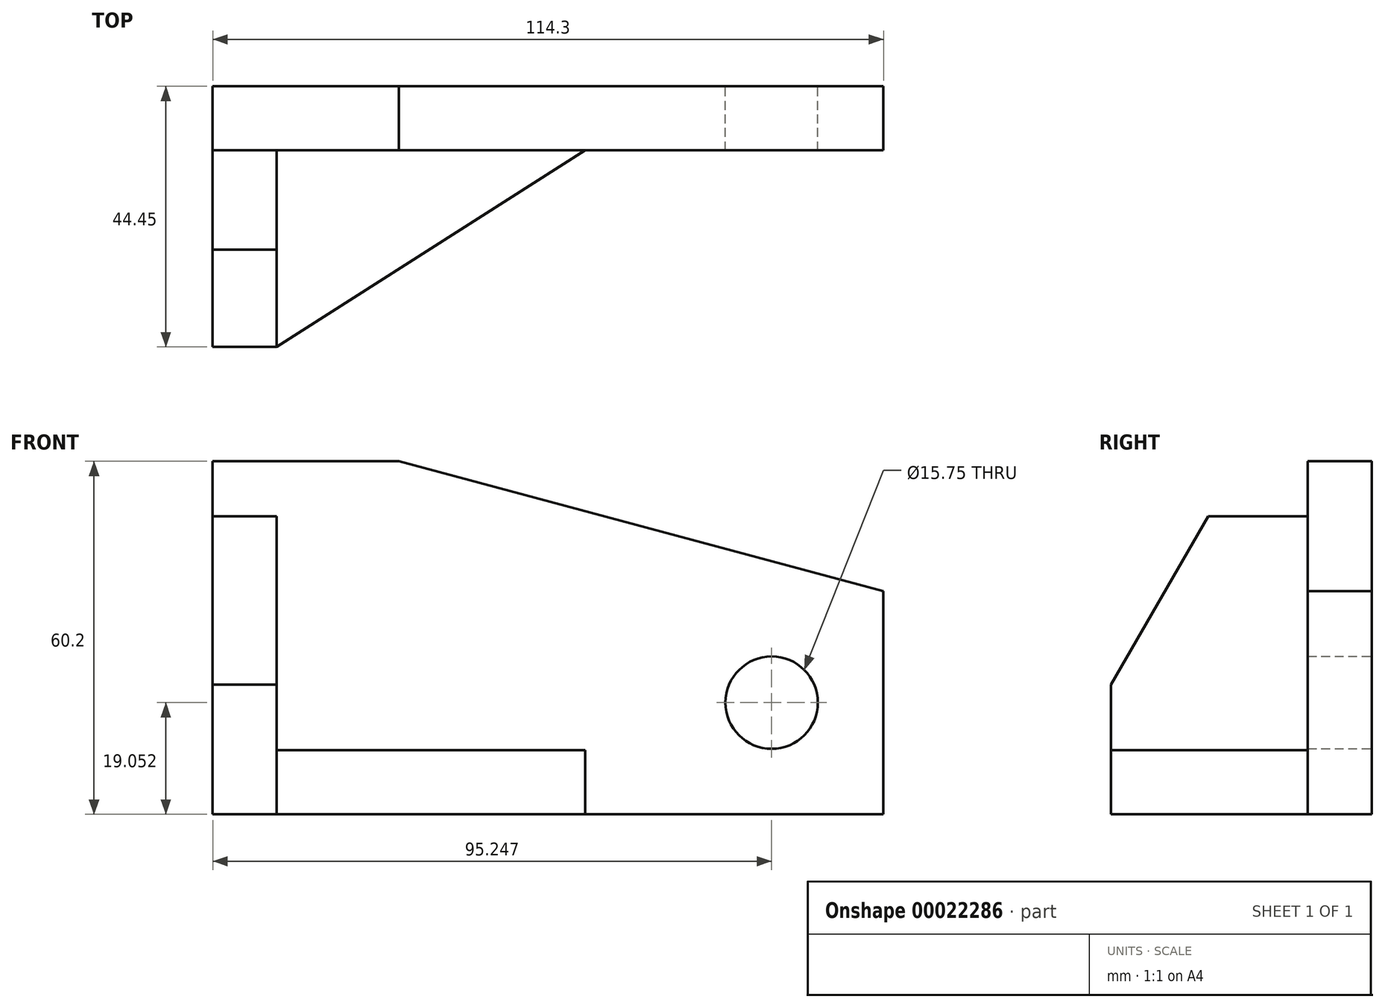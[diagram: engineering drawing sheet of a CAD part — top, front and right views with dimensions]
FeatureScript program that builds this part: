
annotation { "Feature Type Name" : "Feature", "Feature Type Description" : "" }
export const myFeature = defineFeature(function(context is Context, id is Id, definition is map)
    precondition{}
    {
        {
            var Q0;
            Q0=qCreatedBy(makeId("Front.planeOp"),FACE);
            var sketch = newSketch(context, id + "F0", { "sketchPlane" : qUnion([Q0])});
            skLineSegment(sketch, "E0.bottom", {"start": v(-81.32, 43.66) * mm, "end": v(32.98, 43.66) * mm});
            skLineSegment(sketch, "E0.top", {"start": v(-81.32, -16.54) * mm, "end": v(32.98, -16.54) * mm});
            skLineSegment(sketch, "E0.left", {"start": v(-81.32, 43.66) * mm, "end": v(-81.32, -16.54) * mm});
            skLineSegment(sketch, "E0.right", {"start": v(32.98, 43.66) * mm, "end": v(32.98, -16.54) * mm});
            skLineSegment(sketch, "E1", {"start": v(-49.57, 43.66) * mm, "end": v(32.98, 21.54) * mm});
            skCircle(sketch, "E2", {"center": v(13.93, 2.51) * mm, "radius": 7.87 * mm});
            skSolve(sketch);
        }
        {
            var Q0;
            {var subQ2=sQuery(id+"F0.wireOp",EDGE,"E0.top");Q0=makeQuery(id+"F0.imprint","IMPRINT",FACE,{"disambiguationData":[TD([[makeQuery(id+"F0.imprint","IMPRINT",EDGE,{"derivedFrom":subQ2}),1.0]])]});}
            extrude(context, id + "F1", {"entities" : qUnion([Q0]), "depth" : 10.92 * mm});
        }
        {
            var Q0;
            Q0=makeQuery(id+"F1.opExtrude","CAP_FACE",FACE,{"disambiguationData":[OSD([sQuery(id+"F0.wireOp",EDGE,"E0.bottom"),sQuery(id+"F0.wireOp",EDGE,"E0.top"),sQuery(id+"F0.wireOp",EDGE,"E0.left"),sQuery(id+"F0.wireOp",EDGE,"E0.right"),sQuery(id+"F0.wireOp",EDGE,"E1")])],"isStart":false});
            var sketch = newSketch(context, id + "F2", { "sketchPlane" : qUnion([Q0])});
            skLineSegment(sketch, "E3.bottom", {"start": v(-81.32, 34.26) * mm, "end": v(-70.4, 34.26) * mm});
            skLineSegment(sketch, "E3.top", {"start": v(-81.32, -16.54) * mm, "end": v(-70.4, -16.54) * mm});
            skLineSegment(sketch, "E3.left", {"start": v(-81.32, 34.26) * mm, "end": v(-81.32, -16.54) * mm});
            skLineSegment(sketch, "E3.right", {"start": v(-70.4, 34.26) * mm, "end": v(-70.4, -16.54) * mm});
            skSolve(sketch);
        }
        {
            var Q0;
            Q0 = qSketchRegion(id + "F2", true);
            extrude(context, id + "F3", {"entities" : qUnion([Q0]), "operationType" : NewBodyOperationType.ADD, "depth" : 33.53 * mm});
        }
        {
            var Q0;
            Q0=makeQuery(id+"F3.opExtrude","SWEPT_FACE",FACE,{"disambiguationData":[OSD([sQuery(id+"F2.wireOp",EDGE,"E3.right")])]});
            var sketch = newSketch(context, id + "F4", { "sketchPlane" : qUnion([Q0])});
            skLineSegment(sketch, "E4", {"start": v(-27.88, 34.26) * mm, "end": v(-44.45, 5.56) * mm});
            skSolve(sketch);
        }
        {
            var Q0;
            Q0 = qSketchRegion(id + "F4", true);
            var Q1;
            {var subQ2=sQuery(id+"F4.wireOp",EDGE,"E4");Q1=makeQuery(id+"F4.imprint","IMPRINT",FACE,{"disambiguationData":[TD([[makeQuery(id+"F4.imprint","IMPRINT",EDGE,{"derivedFrom":subQ2}),-1.0]])]});}
            extrude(context, id + "F5", {"entities" : qUnion([Q0, Q1]), "operationType" : NewBodyOperationType.REMOVE, "oppositeDirection" : true, "depth" : 25.4 * mm});
        }
        {
            var Q0;
            Q0=makeQuery(id+"F1.opExtrude","CAP_FACE",FACE,{"disambiguationData":[OSD([sQuery(id+"F0.wireOp",EDGE,"E0.bottom"),sQuery(id+"F0.wireOp",EDGE,"E0.top"),sQuery(id+"F0.wireOp",EDGE,"E0.left"),sQuery(id+"F0.wireOp",EDGE,"E0.right"),sQuery(id+"F0.wireOp",EDGE,"E1"),sQuery(id+"F0.wireOp",EDGE,"E2")])],"isStart":false});
            var sketch = newSketch(context, id + "F6", { "sketchPlane" : qUnion([Q0])});
            skLineSegment(sketch, "E5.bottom", {"start": v(-70.4, -16.54) * mm, "end": v(-17.82, -16.54) * mm});
            skLineSegment(sketch, "E5.top", {"start": v(-70.4, -5.62) * mm, "end": v(-17.82, -5.62) * mm});
            skLineSegment(sketch, "E5.left", {"start": v(-70.4, -16.54) * mm, "end": v(-70.4, -5.62) * mm});
            skLineSegment(sketch, "E5.right", {"start": v(-17.82, -16.54) * mm, "end": v(-17.82, -5.62) * mm});
            skSolve(sketch);
        }
        {
            var Q0;
            Q0 = qSketchRegion(id + "F6", true);
            extrude(context, id + "F7", {"entities" : qUnion([Q0]), "operationType" : NewBodyOperationType.ADD, "depth" : 33.53 * mm});
        }
        {
            var Q0;
            Q0=makeQuery(id+"F7.opExtrude","SWEPT_FACE",FACE,{"disambiguationData":[OSD([sQuery(id+"F6.wireOp",EDGE,"E5.top")])]});
            var sketch = newSketch(context, id + "F8", { "sketchPlane" : qUnion([Q0])});
            skLineSegment(sketch, "E6", {"start": v(-70.4, -44.45) * mm, "end": v(-17.82, -10.92) * mm});
            skSolve(sketch);
        }
        {
            var Q0;
            Q0 = qSketchRegion(id + "F8", true);
            var Q1;
            Q1=makeQuery(id+"F8.imprint","IMPRINT",FACE,{"disambiguationData":[TD([[makeQuery(id+"F8.imprint","IMPRINT",EDGE,{"derivedFrom":sQuery(id+"F8.wireOp",EDGE,"E6")}),-1.0]])]});
            extrude(context, id + "F9", {"entities" : qUnion([Q0, Q1]), "operationType" : NewBodyOperationType.REMOVE, "oppositeDirection" : true, "depth" : 25.4 * mm});
        }
    });
